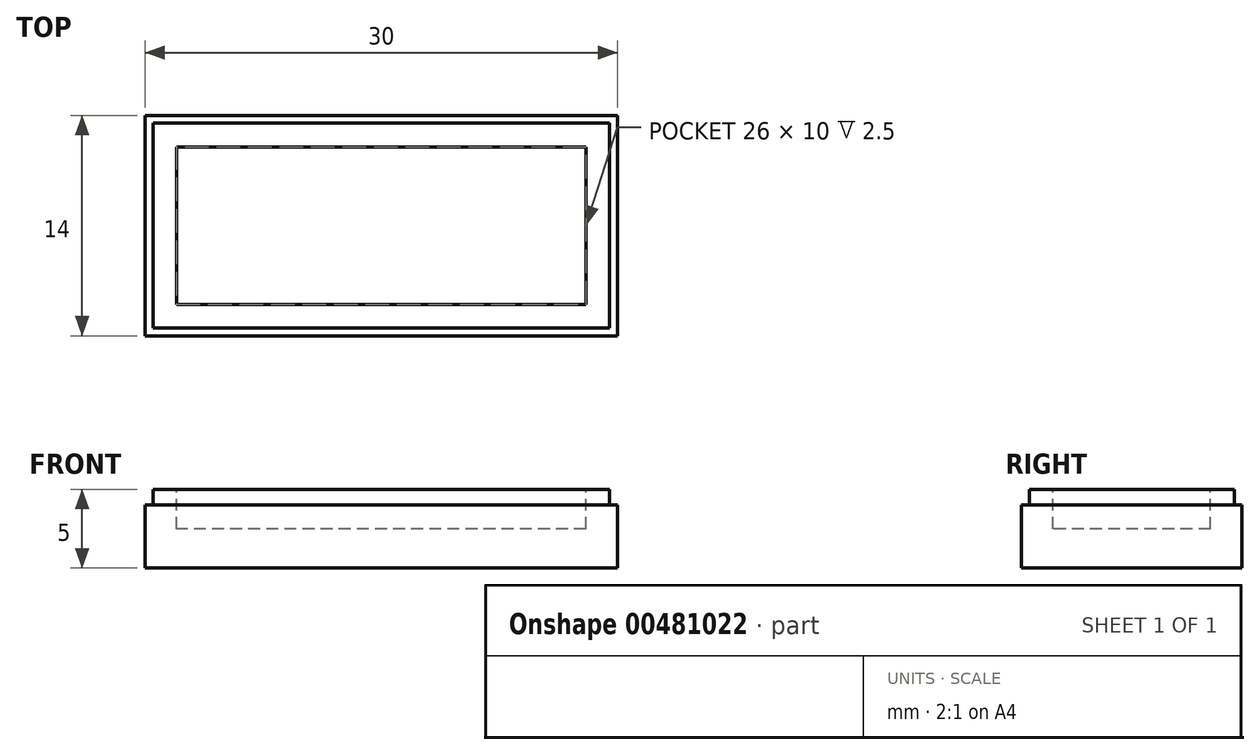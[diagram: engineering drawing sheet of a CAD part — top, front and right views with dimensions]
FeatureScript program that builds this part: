
annotation { "Feature Type Name" : "Feature", "Feature Type Description" : "" }
export const myFeature = defineFeature(function(context is Context, id is Id, definition is map)
    precondition{}
    {
        {
            var Q0;
            Q0=qCreatedBy(makeId("Top.planeOp"),FACE);
            var sketch = newSketch(context, id + "F0", { "sketchPlane" : qUnion([Q0])});
            skLineSegment(sketch, "E0.bottom", {"start": v(9.44, -9.93) * mm, "end": v(-20.56, -9.93) * mm});
            skLineSegment(sketch, "E0.top", {"start": v(9.44, -23.93) * mm, "end": v(-20.56, -23.93) * mm});
            skLineSegment(sketch, "E0.left", {"start": v(9.44, -9.93) * mm, "end": v(9.44, -23.93) * mm});
            skLineSegment(sketch, "E0.right", {"start": v(-20.56, -9.93) * mm, "end": v(-20.56, -23.93) * mm});
            skPoint(sketch, "E0.middle", {"position": v(-5.56, -16.93) * mm});
            skLineSegment(sketch, "E1", {"start": v(-20.56, -9.93) * mm, "end": v(9.44, -23.93) * mm, "construction": true});
            skLineSegment(sketch, "E2", {"start": v(9.44, -9.93) * mm, "end": v(-20.56, -23.93) * mm, "construction": true});
            skSolve(sketch);
        }
        {
            var Q0;
            Q0 = qSketchRegion(id + "F0", true);
            extrude(context, id + "F1", {"entities" : qUnion([Q0]), "depth" : 4 * mm});
        }
        {
            var Q0;
            Q0=makeQuery(id+"F1.opExtrude","CAP_FACE",FACE,{"disambiguationData":[OSD([sQuery(id+"F0.wireOp",EDGE,"E0.bottom"),sQuery(id+"F0.wireOp",EDGE,"E0.top"),sQuery(id+"F0.wireOp",EDGE,"E0.left"),sQuery(id+"F0.wireOp",EDGE,"E0.right")])],"isStart":false});
            var sketch = newSketch(context, id + "F2", { "sketchPlane" : qUnion([Q0])});
            skLineSegment(sketch, "E3.0", {"start": v(8.94, -10.43) * mm, "end": v(-20.06, -10.43) * mm});
            skLineSegment(sketch, "E3.1", {"start": v(8.94, -10.43) * mm, "end": v(8.94, -23.43) * mm});
            skLineSegment(sketch, "E3.2", {"start": v(8.94, -23.43) * mm, "end": v(-20.06, -23.43) * mm});
            skLineSegment(sketch, "E3.3", {"start": v(-20.06, -10.43) * mm, "end": v(-20.06, -23.43) * mm});
            skSolve(sketch);
        }
        {
            var Q0;
            Q0=makeQuery(id+"F2.imprint","IMPRINT",FACE,{"disambiguationData":[TD([[makeQuery(id+"F2.imprint","IMPRINT",EDGE,{"derivedFrom":sQuery(id+"F2.wireOp",EDGE,"E3.0")}),1.0]])]});
            extrude(context, id + "F3", {"entities" : qUnion([Q0]), "operationType" : NewBodyOperationType.ADD, "depth" : 1 * mm});
        }
        {
            var Q0;
            Q0=makeQuery(id+"F3.opExtrude","CAP_FACE",FACE,{"disambiguationData":[OSD([sQuery(id+"F2.wireOp",EDGE,"E3.0"),sQuery(id+"F2.wireOp",EDGE,"E3.1"),sQuery(id+"F2.wireOp",EDGE,"E3.2"),sQuery(id+"F2.wireOp",EDGE,"E3.3")])],"isStart":false});
            var sketch = newSketch(context, id + "F4", { "sketchPlane" : qUnion([Q0])});
            skLineSegment(sketch, "E4.0", {"start": v(7.44, -11.93) * mm, "end": v(-18.56, -11.93) * mm});
            skLineSegment(sketch, "E4.1", {"start": v(7.44, -11.93) * mm, "end": v(7.44, -21.93) * mm});
            skLineSegment(sketch, "E4.2", {"start": v(7.44, -21.93) * mm, "end": v(-18.56, -21.93) * mm});
            skLineSegment(sketch, "E4.3", {"start": v(-18.56, -11.93) * mm, "end": v(-18.56, -21.93) * mm});
            skSolve(sketch);
        }
        {
            var Q0;
            Q0=makeQuery(id+"F4.imprint","IMPRINT",FACE,{"disambiguationData":[TD([[makeQuery(id+"F4.imprint","IMPRINT",EDGE,{"derivedFrom":sQuery(id+"F4.wireOp",EDGE,"E4.0")}),1.0]])]});
            extrude(context, id + "F5", {"entities" : qUnion([Q0]), "operationType" : NewBodyOperationType.REMOVE, "oppositeDirection" : true, "depth" : 2.5 * mm});
        }
    });
